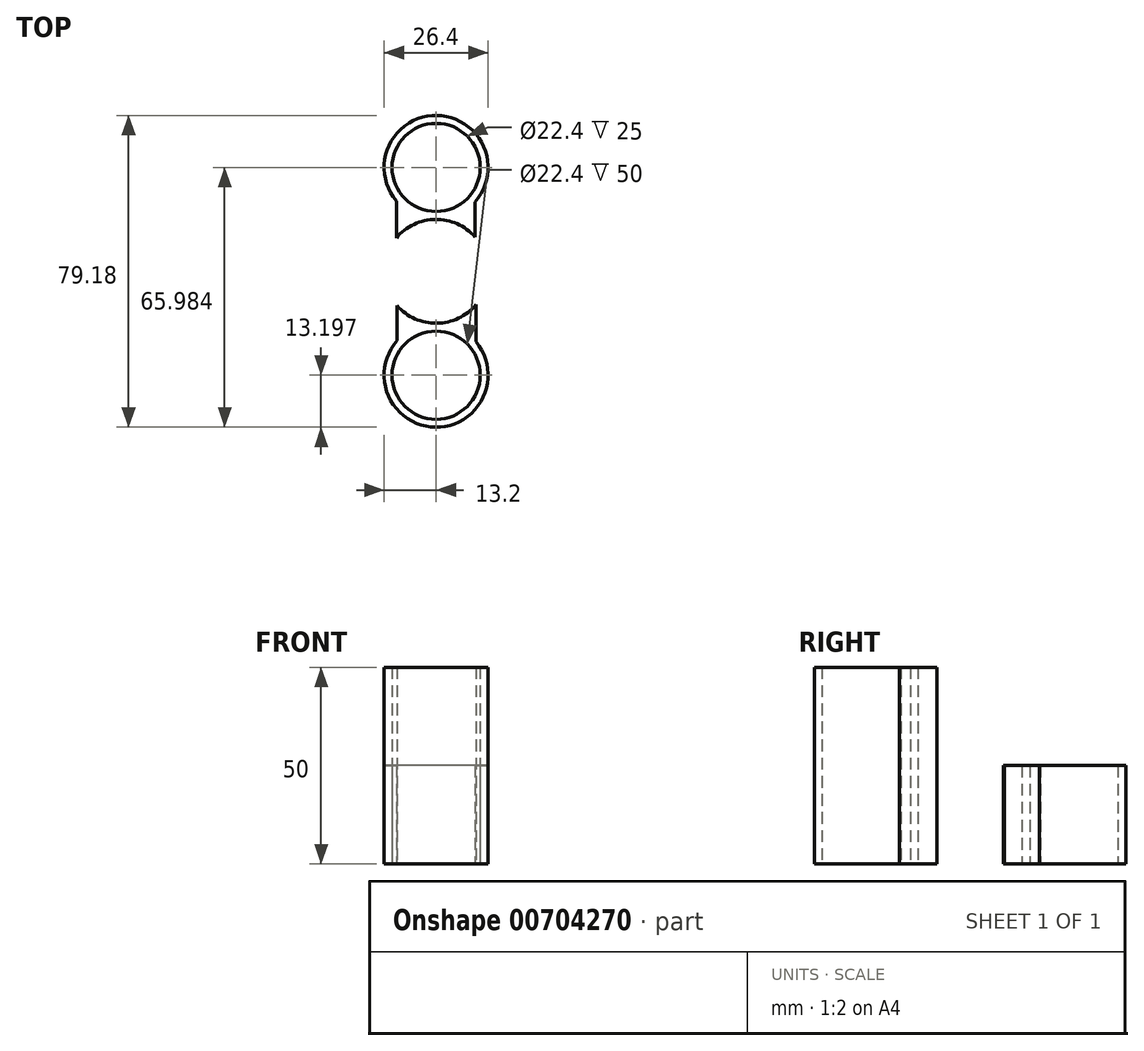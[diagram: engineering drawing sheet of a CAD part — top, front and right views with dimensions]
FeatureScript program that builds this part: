
annotation { "Feature Type Name" : "Feature", "Feature Type Description" : "" }
export const myFeature = defineFeature(function(context is Context, id is Id, definition is map)
    precondition{}
    {
        {
            var Q0;
            Q0=qCreatedBy(makeId("Top.planeOp"),FACE);
            var sketch = newSketch(context, id + "F0", { "sketchPlane" : qUnion([Q0])});
            skCircle(sketch, "E0", {"center": v(0, 0) * mm, "radius": 11.2 * mm});
            skCircle(sketch, "E1", {"center": v(0, 0) * mm, "radius": 13.2 * mm});
            skCircle(sketch, "E2", {"center": v(0, 26.4) * mm, "radius": 11.2 * mm});
            skArc(sketch, "E3", {"start": v(-0.3, 13.2) * mm, "mid": v(0, 13.2) * mm, "end": v(0.3, 13.2) * mm});
            skArc(sketch, "E4.1.0", {"start": v(0.3, -13.2) * mm, "mid": v(0, -13.2) * mm, "end": v(-0.3, -13.2) * mm});
            skCircle(sketch, "E4.1.1", {"center": v(0, -26.4) * mm, "radius": 11.2 * mm});
            skLineSegment(sketch, "E5", {"start": v(-10.1, 17.9) * mm, "end": v(-10.1, 8.5) * mm});
            skLineSegment(sketch, "E6.1.0", {"start": v(10.1, -17.9) * mm, "end": v(10.1, -8.5) * mm});
            skLineSegment(sketch, "E7", {"start": v(9.88, 17.64) * mm, "end": v(9.88, 8.75) * mm});
            skLineSegment(sketch, "E8", {"start": v(9.88, 8.75) * mm, "end": v(15.9, -6.24) * mm});
            skLineSegment(sketch, "E9.1.0", {"start": v(-9.88, -17.64) * mm, "end": v(-9.88, -8.75) * mm});
            skArc(sketch, "E10.trimOffspring", {"start": v(-9.88, -17.64) * mm, "mid": v(-0.17, -39.6) * mm, "end": v(10.1, -17.9) * mm});
            skArc(sketch, "E11.trimOffspring", {"start": v(9.88, 17.64) * mm, "mid": v(0.17, 39.6) * mm, "end": v(-10.1, 17.9) * mm});
            skSolve(sketch);
        }
        {
            var Q0;
            Q0=makeQuery(id+"F0.imprint","IMPRINT",FACE,{"disambiguationData":[TD([[makeQuery(id+"F0.imprint","IMPRINT",EDGE,{"derivedFrom":sQuery(id+"F0.wireOp",EDGE,"E4.1.1")}),-1.0]])]});
            var Q1;
            Q1=makeQuery(id+"F0.imprint","IMPRINT",FACE,{"disambiguationData":[TD([[makeQuery(id+"F0.imprint","IMPRINT",EDGE,{"derivedFrom":sQuery(id+"F0.wireOp",EDGE,"E2")}),-1.0]])]});
            extrude(context, id + "F1", {"entities" : qUnion([Q0, Q1]), "depth" : 25 * mm, "offsetDistance" : 25 * mm});
        }
        {
            var Q0;
            Q0=makeQuery(id+"F1.opExtrude","CAP_FACE",FACE,{"disambiguationData":[OSD([sQuery(id+"F0.wireOp",EDGE,"E1"),sQuery(id+"F0.wireOp",EDGE,"E4.1.1"),sQuery(id+"F0.wireOp",EDGE,"E6.1.0"),sQuery(id+"F0.wireOp",EDGE,"E9.1.0"),sQuery(id+"F0.wireOp",EDGE,"E10.trimOffspring")])],"isStart":false});
            extrude(context, id + "F2", {"entities" : qUnion([Q0]), "operationType" : NewBodyOperationType.ADD, "depth" : 25 * mm, "offsetDistance" : 25 * mm});
        }
    });
